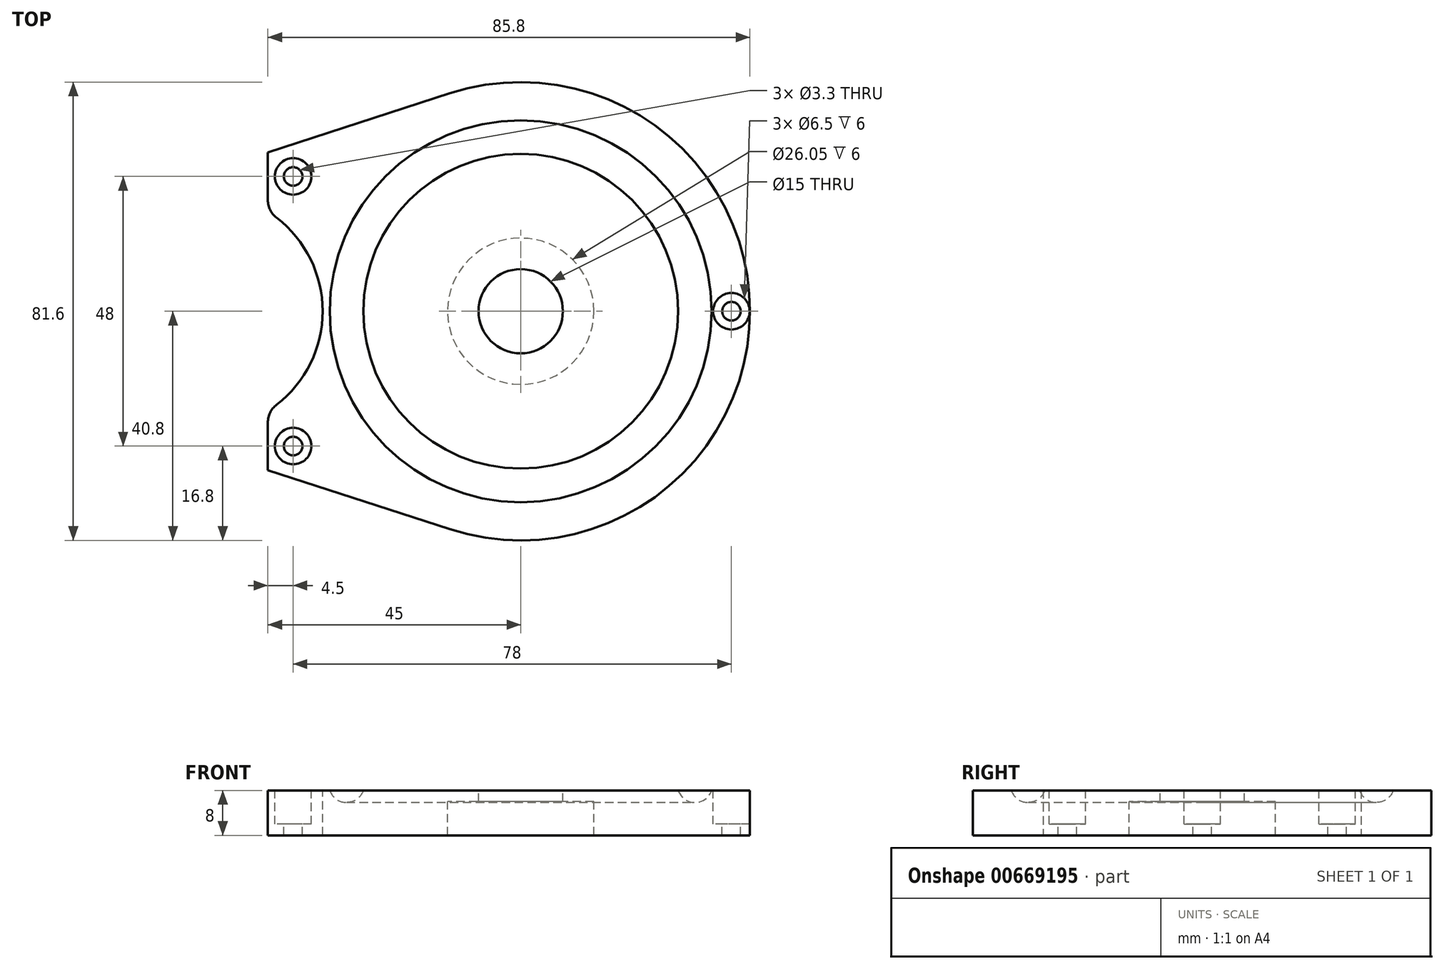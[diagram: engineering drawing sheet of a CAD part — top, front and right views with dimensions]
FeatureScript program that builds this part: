
annotation { "Feature Type Name" : "Feature", "Feature Type Description" : "" }
export const myFeature = defineFeature(function(context is Context, id is Id, definition is map)
    precondition{}
    {
        {
            var Q0;
            Q0=qCreatedBy(makeId("Top.planeOp"),FACE);
            var sketch = newSketch(context, id + "F0", { "sketchPlane" : qUnion([Q0])});
            skCircle(sketch, "E0", {"center": v(0, 0) * mm, "radius": 40.8 * mm});
            skSolve(sketch);
        }
        {
            var Q0;
            Q0=qSketchRegion(id+"F0",true);
            extrude(context, id + "F1", {"entities" : qUnion([Q0]), "depth" : 8 * mm, "offsetDistance" : 25 * mm});
        }
        {
            var Q0;
            Q0=qCreatedBy(makeId("Right.planeOp"),FACE);
            var sketch = newSketch(context, id + "F2", { "sketchPlane" : qUnion([Q0])});
            skLineSegment(sketch, "E1", {"start": v(0, 0) * mm, "end": v(0, 8) * mm});
            skLineSegment(sketch, "E2", {"start": v(0, 8) * mm, "end": v(7.5, 8) * mm});
            skLineSegment(sketch, "E3", {"start": v(7.5, 8) * mm, "end": v(7.5, 6) * mm});
            skLineSegment(sketch, "E4", {"start": v(7.5, 6) * mm, "end": v(13.03, 6) * mm});
            skLineSegment(sketch, "E5", {"start": v(13.03, 6) * mm, "end": v(13.03, 0) * mm});
            skLineSegment(sketch, "E6", {"start": v(13.03, 0) * mm, "end": v(0, 0) * mm});
            skLineSegment(sketch, "E7", {"start": v(0, 8) * mm, "end": v(0, 13.47) * mm, "construction": true});
            skSolve(sketch);
        }
        {
            var Q0;
            Q0=qSketchRegion(id+"F2",true);
            var Q1;
            Q1=sQuery(id+"F2.wireOp",EDGE,"E7");
            revolve(context, id + "F3", {"operationType" : NewBodyOperationType.REMOVE, "entities" : qUnion([Q0]), "axis" : qUnion([Q1]), "revolveType" : RevolveType.FULL, "oppositeDirection" : true});
        }
        {
            var Q0;
            Q0=qCreatedBy(makeId("Right.planeOp"),FACE);
            var sketch = newSketch(context, id + "F4", { "sketchPlane" : qUnion([Q0])});
            skCircle(sketch, "E8", {"center": v(31, 9) * mm, "radius": 3.15 * mm});
            skLineSegment(sketch, "E9", {"start": v(0, -0.8) * mm, "end": v(0, 13.57) * mm, "construction": true});
            skSolve(sketch);
        }
        {
            var Q0;
            Q0=qSketchRegion(id+"F4",true);
            var Q1;
            Q1=sQuery(id+"F4.wireOp",EDGE,"E9");
            revolve(context, id + "F5", {"operationType" : NewBodyOperationType.REMOVE, "entities" : qUnion([Q0]), "axis" : qUnion([Q1]), "revolveType" : RevolveType.FULL, "oppositeDirection" : true});
        }
        {
            var Q0;
            Q0=qCreatedBy(makeId("Top.planeOp"),FACE);
            var sketch = newSketch(context, id + "F6", { "sketchPlane" : qUnion([Q0])});
            skLineSegment(sketch, "E10.bottom", {"start": v(-36, 19.2) * mm, "end": v(-40.8, 19.2) * mm});
            skLineSegment(sketch, "E10.top", {"start": v(-36, -19.2) * mm, "end": v(-40.8, -19.2) * mm});
            skLineSegment(sketch, "E10.left", {"start": v(-36, 19.2) * mm, "end": v(-36, -19.2) * mm});
            skLineSegment(sketch, "E10.right", {"start": v(-40.8, 19.2) * mm, "end": v(-40.8, -19.2) * mm});
            skSolve(sketch);
        }
        {
            var Q0;
            Q0=qSketchRegion(id+"F6",true);
            extrude(context, id + "F7", {"entities" : qUnion([Q0]), "operationType" : NewBodyOperationType.REMOVE, "endBound" : BoundingType.THROUGH_ALL, "depth" : 25 * mm});
        }
        {
            var Q0;
            Q0=qCreatedBy(makeId("Top.planeOp"),FACE);
            var sketch = newSketch(context, id + "F8", { "sketchPlane" : qUnion([Q0])});
            skLineSegment(sketch, "E11", {"start": v(-45, -28.28) * mm, "end": v(-45, 28.28) * mm});
            skLineSegment(sketch, "E12", {"start": v(-45, 28.28) * mm, "end": v(-12.6, 38.8) * mm});
            skLineSegment(sketch, "E13", {"start": v(0, 0) * mm, "end": v(-51.86, 0) * mm, "construction": true});
            skArc(sketch, "E14.0", {"start": v(-12.6, 38.8) * mm, "mid": v(-26.2, 31.27) * mm, "end": v(-36, 19.2) * mm});
            skPoint(sketch, "E15.orphan", {"position": v(-36, -19.2) * mm});
            skLineSegment(sketch, "E16.MirrorCS", {"start": v(-45, -28.28) * mm, "end": v(-12.6, -38.8) * mm});
            skArc(sketch, "E17.MirrorCS", {"start": v(-12.6, -38.8) * mm, "mid": v(-26.2, -31.27) * mm, "end": v(-36, -19.2) * mm});
            skLineSegment(sketch, "E18", {"start": v(-36, 19.2) * mm, "end": v(-36, -19.2) * mm});
            skSolve(sketch);
        }
        {
            var Q0;
            Q0=qSketchRegion(id+"F8",true);
            var Q1;
            {var subQ0=sQuery(id+"F0.wireOp",EDGE,"E0");Q1=makeQuery(id+"F5.boolean.opBoolean","SPLIT",FACE,{"disambiguationData":[TD([makeQuery(id+"F1.opExtrude","SWEPT_FACE",FACE,{"disambiguationData":[OSD([subQ0])]})])],"derivedFrom":makeQuery(id+"F1.opExtrude","CAP_FACE",FACE,{"disambiguationData":[OSD([subQ0])],"isStart":false})});}
            extrude(context, id + "F9", {"entities" : qUnion([Q0]), "operationType" : NewBodyOperationType.ADD, "endBound" : BoundingType.UP_TO_SURFACE, "endBoundEntityFace" : qUnion([Q1]), "depth" : 25 * mm});
        }
        {
            var Q0;
            {var subQ0=sQuery(id+"F0.wireOp",EDGE,"E0");Q0=makeQuery(id+"F9.boolean.opBoolean","MERGE",FACE,{"derivedFrom":[makeQuery(id+"F5.boolean.opBoolean","SPLIT",FACE,{"disambiguationData":[TD([makeQuery(id+"F1.opExtrude","SWEPT_FACE",FACE,{"disambiguationData":[OSD([subQ0])]})])],"derivedFrom":makeQuery(id+"F1.opExtrude","CAP_FACE",FACE,{"disambiguationData":[OSD([subQ0])],"isStart":false})}),makeQuery(id+"F9.opExtrude","CAP_FACE",FACE,{"disambiguationData":[OSD([sQuery(id+"F8.wireOp",EDGE,"E11"),sQuery(id+"F8.wireOp",EDGE,"E12"),sQuery(id+"F8.wireOp",EDGE,"E14.0"),sQuery(id+"F8.wireOp",EDGE,"E16.MirrorCS"),sQuery(id+"F8.wireOp",EDGE,"E17.MirrorCS"),sQuery(id+"F8.wireOp",EDGE,"E18")])],"isStart":false})]});}
            var sketch = newSketch(context, id + "F10", { "sketchPlane" : qUnion([Q0])});
            skCircle(sketch, "E19", {"center": v(-56.25, 0) * mm, "radius": 21 * mm});
            skLineSegment(sketch, "E20", {"start": v(-56.25, 0) * mm, "end": v(0, 0) * mm, "construction": true});
            skSolve(sketch);
        }
        {
            var Q0;
            Q0=qSketchRegion(id+"F10",true);
            extrude(context, id + "F11", {"entities" : qUnion([Q0]), "operationType" : NewBodyOperationType.REMOVE, "endBound" : BoundingType.THROUGH_ALL, "oppositeDirection" : true, "depth" : 25 * mm});
        }
        {
            var Q0;
            Q0=makeQuery(id+"F11.boolean.opBoolean","INTERSECT",EDGE,{"disambiguationData":[OD(1.0)],"derivedFrom":[makeQuery(id+"F9.opExtrude","SWEPT_FACE",FACE,{"disambiguationData":[OSD([sQuery(id+"F8.wireOp",EDGE,"E11")])]}),makeQuery(id+"F11.opExtrude","SWEPT_FACE",FACE,{"disambiguationData":[OSD([sQuery(id+"F10.wireOp",EDGE,"E19")])]})]});
            var Q1;
            Q1=makeQuery(id+"F11.boolean.opBoolean","INTERSECT",EDGE,{"disambiguationData":[OD(0.0)],"derivedFrom":[makeQuery(id+"F9.opExtrude","SWEPT_FACE",FACE,{"disambiguationData":[OSD([sQuery(id+"F8.wireOp",EDGE,"E11")])]}),makeQuery(id+"F11.opExtrude","SWEPT_FACE",FACE,{"disambiguationData":[OSD([sQuery(id+"F10.wireOp",EDGE,"E19")])]})]});
            fillet(context, id + "F12", {"entities" : qUnion([Q0, Q1]), "radius" : 4 * mm, "tangentPropagation" : true, "allowEdgeOverflow" : false});
        }
        {
            var Q0;
            {var subQ0=sQuery(id+"F0.wireOp",EDGE,"E0");Q0=makeQuery(id+"F9.boolean.opBoolean","MERGE",FACE,{"derivedFrom":[makeQuery(id+"F5.boolean.opBoolean","SPLIT",FACE,{"disambiguationData":[TD([makeQuery(id+"F1.opExtrude","SWEPT_FACE",FACE,{"disambiguationData":[OSD([subQ0])]})])],"derivedFrom":makeQuery(id+"F1.opExtrude","CAP_FACE",FACE,{"disambiguationData":[OSD([subQ0])],"isStart":false})}),makeQuery(id+"F9.opExtrude","CAP_FACE",FACE,{"disambiguationData":[OSD([sQuery(id+"F8.wireOp",EDGE,"E11"),sQuery(id+"F8.wireOp",EDGE,"E12"),sQuery(id+"F8.wireOp",EDGE,"E14.0"),sQuery(id+"F8.wireOp",EDGE,"E16.MirrorCS"),sQuery(id+"F8.wireOp",EDGE,"E17.MirrorCS"),sQuery(id+"F8.wireOp",EDGE,"E18")])],"isStart":false})]});}
            var sketch = newSketch(context, id + "F13", { "sketchPlane" : qUnion([Q0])});
            skPoint(sketch, "E21", {"position": v(-40.5, 24) * mm});
            skPoint(sketch, "E22", {"position": v(37.5, 0) * mm});
            skLineSegment(sketch, "E23", {"start": v(0, 0) * mm, "end": v(47.97, 0) * mm, "construction": true});
            skPoint(sketch, "E24.MirrorP", {"position": v(-40.5, -24) * mm});
            skSolve(sketch);
        }
        {
            var Q0;
            Q0=sQuery(id+"F13.wireOp",VERTEX,"E21");
            var Q1;
            Q1=sQuery(id+"F13.wireOp",VERTEX,"E24.MirrorP");
            var Q2;
            Q2=sQuery(id+"F13.wireOp",VERTEX,"E22");
            var Q3;
            Q3=makeQuery(id+"F1.opExtrude","SWEPT_BODY",BODY,{"disambiguationData":[OSD([sQuery(id+"F0.wireOp",EDGE,"E0")])]});
            hole(context, id + "F14", {"style" : HoleStyle.C_BORE, "endStyle" : HoleEndStyle.THROUGH, "holeDiameter" : 3.3 * mm, "cBoreDiameter" : 6.5 * mm, "cBoreDepth" : 6 * mm, "tappedDepth" : 12 * mm, "tapClearance" : 3, "locations" : qUnion([Q0, Q1, Q2]), "scope" : qUnion([Q3]), "majorDiameter" : 5 * mm});
        }
    });
